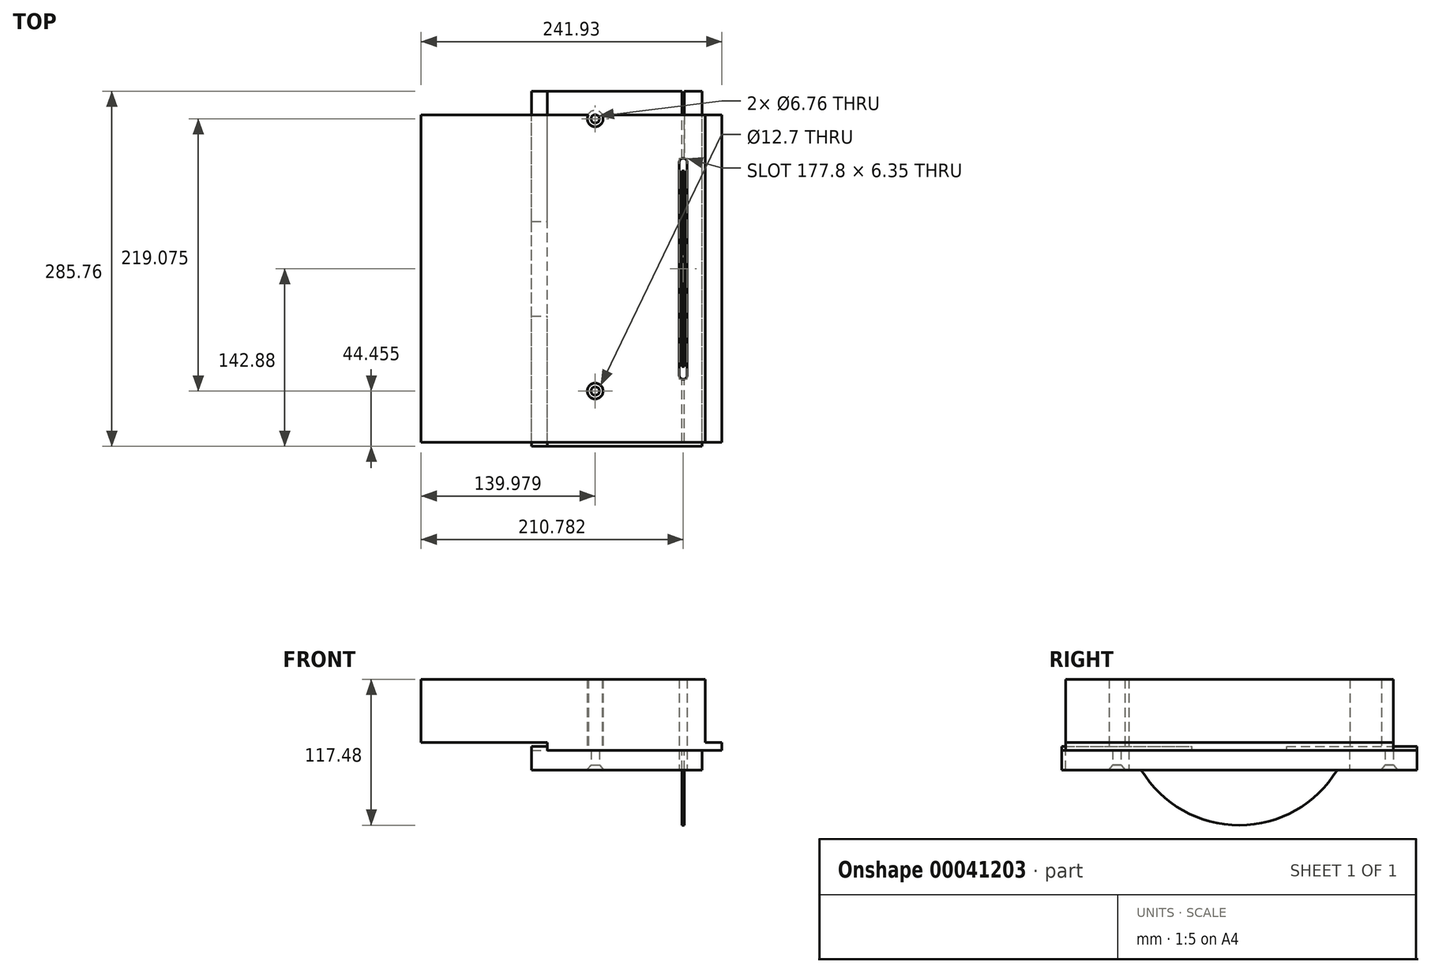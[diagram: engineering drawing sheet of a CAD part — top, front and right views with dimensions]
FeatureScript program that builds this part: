
annotation { "Feature Type Name" : "Feature", "Feature Type Description" : "" }
export const myFeature = defineFeature(function(context is Context, id is Id, definition is map)
    precondition{}
    {
        {
            var Q0;
            Q0=qCreatedBy(makeId("Front.planeOp"),FACE);
            var sketch = newSketch(context, id + "F0", { "sketchPlane" : qUnion([Q0])});
            skLineSegment(sketch, "E0.bottom", {"start": v(0, 0) * mm, "end": v(140.34, 0) * mm});
            skLineSegment(sketch, "E0.top", {"start": v(0, 6.35) * mm, "end": v(140.34, 6.35) * mm});
            skLineSegment(sketch, "E0.left", {"start": v(0, 0) * mm, "end": v(0, 6.35) * mm});
            skLineSegment(sketch, "E0.right", {"start": v(140.34, 0) * mm, "end": v(140.34, 6.35) * mm});
            skLineSegment(sketch, "E1.bottom", {"start": v(127, 6.35) * mm, "end": v(-101.6, 6.35) * mm});
            skLineSegment(sketch, "E1.top", {"start": v(127, 57.15) * mm, "end": v(-101.6, 57.15) * mm});
            skLineSegment(sketch, "E1.left", {"start": v(127, 6.35) * mm, "end": v(127, 57.15) * mm});
            skLineSegment(sketch, "E1.right", {"start": v(-101.6, 6.35) * mm, "end": v(-101.6, 57.15) * mm});
            skLineSegment(sketch, "E2.bottom", {"start": v(108.23, 0) * mm, "end": v(110.13, 0) * mm});
            skLineSegment(sketch, "E2.top", {"start": v(108.23, -60.96) * mm, "end": v(110.13, -60.96) * mm});
            skLineSegment(sketch, "E2.left", {"start": v(108.23, 0) * mm, "end": v(108.23, -60.96) * mm});
            skLineSegment(sketch, "E2.right", {"start": v(110.13, 0) * mm, "end": v(110.13, -60.96) * mm});
            skSolve(sketch);
        }
        {
            var Q0;
            Q0=qSketchRegion(id+"F0",true);
            extrude(context, id + "F1", {"entities" : qUnion([Q0]), "depth" : 139.7 * mm, "hasSecondDirection" : true, "secondDirectionOppositeDirection" : true, "secondDirectionDepth" : 123.82 * mm});
        }
        {
            var Q0;
            Q0=qCreatedBy(makeId("Front.planeOp"),FACE);
            var sketch = newSketch(context, id + "F2", { "sketchPlane" : qUnion([Q0])});
            skLineSegment(sketch, "E3.bottom", {"start": v(0, 0) * mm, "end": v(124.46, 0) * mm});
            skLineSegment(sketch, "E3.top", {"start": v(0, -15.88) * mm, "end": v(124.46, -15.88) * mm});
            skLineSegment(sketch, "E3.left", {"start": v(0, 0) * mm, "end": v(0, -15.88) * mm});
            skLineSegment(sketch, "E3.right", {"start": v(124.46, 0) * mm, "end": v(124.46, -15.88) * mm});
            skLineSegment(sketch, "E4.bottom", {"start": v(0, -15.88) * mm, "end": v(-12.7, -15.88) * mm});
            skLineSegment(sketch, "E4.top", {"start": v(0, 3.18) * mm, "end": v(-12.7, 3.17) * mm});
            skLineSegment(sketch, "E4.left", {"start": v(0, -15.88) * mm, "end": v(0, 3.18) * mm});
            skLineSegment(sketch, "E4.right", {"start": v(-12.7, -15.88) * mm, "end": v(-12.7, 3.17) * mm});
            skSolve(sketch);
        }
        {
            var Q0;
            Q0=makeQuery(id+"F2.imprint","IMPRINT",FACE,{"disambiguationData":[TD([[makeQuery(id+"F2.imprint","IMPRINT",EDGE,{"derivedFrom":sQuery(id+"F2.wireOp",EDGE,"E3.bottom")}),-1.0]])]});
            var Q1;
            {var subQ3=sQuery(id+"F2.wireOp",EDGE,"E4.bottom");Q1=makeQuery(id+"F2.imprint","IMPRINT",FACE,{"disambiguationData":[TD([[makeQuery(id+"F2.imprint","IMPRINT",EDGE,{"derivedFrom":subQ3}),-1.0]])]});}
            var Q2;
            Q2=makeQuery(id+"F1.opExtrude","CAP_FACE",FACE,{"disambiguationData":[OSD([sQuery(id+"F0.wireOp",EDGE,"E0.bottom"),sQuery(id+"F0.wireOp",EDGE,"E0.top"),sQuery(id+"F0.wireOp",EDGE,"E0.left"),sQuery(id+"F0.wireOp",EDGE,"E0.right"),sQuery(id+"F0.wireOp",EDGE,"E1.bottom"),sQuery(id+"F0.wireOp",EDGE,"E1.top"),sQuery(id+"F0.wireOp",EDGE,"E1.left"),sQuery(id+"F0.wireOp",EDGE,"E1.right"),sQuery(id+"F0.wireOp",EDGE,"E2.top"),sQuery(id+"F0.wireOp",EDGE,"E2.left"),sQuery(id+"F0.wireOp",EDGE,"E2.right")])],"isStart":true});
            extrude(context, id + "F3", {"entities" : qUnion([Q0, Q1]), "depth" : 142.88 * mm, "hasSecondDirection" : true, "secondDirectionOppositeDirection" : true, "secondDirectionBoundEntityFace" : qUnion([Q2]), "secondDirectionDepth" : 142.88 * mm});
        }
        {
            var Q0;
            Q0=makeQuery(id+"F3.opExtrude","SWEPT_FACE",FACE,{"disambiguationData":[OSD([sQuery(id+"F2.wireOp",EDGE,"E3.top")])]});
            var sketch = newSketch(context, id + "F4", { "sketchPlane" : qUnion([Q0])});
            skLineSegment(sketch, "E5.bottom", {"start": v(109.18, -88.9) * mm, "end": v(109.18, -88.9) * mm});
            skLineSegment(sketch, "E5.top", {"start": v(109.18, 88.9) * mm, "end": v(109.18, 88.9) * mm});
            skLineSegment(sketch, "E5.left", {"start": v(112.36, 85.73) * mm, "end": v(112.36, -85.73) * mm});
            skLineSegment(sketch, "E5.right", {"start": v(106, 85.73) * mm, "end": v(106, -85.73) * mm});
            skArc(sketch, "E6.filletArc", {"start": v(109.18, 88.9) * mm, "mid": v(106.94, 87.97) * mm, "end": v(106, 85.73) * mm});
            skArc(sketch, "E7.filletArc", {"start": v(112.36, 85.73) * mm, "mid": v(111.43, 87.97) * mm, "end": v(109.18, 88.9) * mm});
            skArc(sketch, "E8.filletArc", {"start": v(109.18, -88.9) * mm, "mid": v(111.43, -87.97) * mm, "end": v(112.36, -85.73) * mm});
            skArc(sketch, "E9.filletArc", {"start": v(106, -85.73) * mm, "mid": v(106.94, -87.97) * mm, "end": v(109.18, -88.9) * mm});
            skSolve(sketch);
        }
        {
            var Q0;
            Q0=makeQuery(id+"F1.opExtrude","SWEPT_FACE",FACE,{"disambiguationData":[OSD([sQuery(id+"F0.wireOp",EDGE,"E2.right")])]});
            var sketch = newSketch(context, id + "F5", { "sketchPlane" : qUnion([Q0])});
            skLineSegment(sketch, "E10.0", {"start": v(-139.7, 0) * mm, "end": v(-139.7, -60.96) * mm});
            skLineSegment(sketch, "E11.0", {"start": v(123.83, 0) * mm, "end": v(123.83, -60.96) * mm});
            skLineSegment(sketch, "E12", {"start": v(0, 0) * mm, "end": v(0, 82.53) * mm, "construction": true});
            skLineSegment(sketch, "E13", {"start": v(-86.43, 0) * mm, "end": v(-139.7, 0) * mm});
            skLineSegment(sketch, "E14", {"start": v(-139.7, 0) * mm, "end": v(-139.7, -88.9) * mm});
            skLineSegment(sketch, "E15", {"start": v(-139.7, -88.9) * mm, "end": v(152.4, -88.9) * mm});
            skLineSegment(sketch, "E16", {"start": v(152.4, -88.9) * mm, "end": v(152.4, 0) * mm});
            skLineSegment(sketch, "E17", {"start": v(152.4, 0) * mm, "end": v(86.43, 0) * mm});
            skArc(sketch, "E18.converted", {"start": v(-86.43, 0) * mm, "mid": v(0, -60.33) * mm, "end": v(86.43, 0) * mm});
            skSolve(sketch);
        }
        {
            var Q0;
            Q0=qSketchRegion(id+"F5",true);
            var Q1;
            Q1=makeQuery(id+"F1.opExtrude","SWEPT_FACE",FACE,{"disambiguationData":[OSD([sQuery(id+"F0.wireOp",EDGE,"E2.left")])]});
            extrude(context, id + "F6", {"entities" : qUnion([Q0]), "operationType" : NewBodyOperationType.REMOVE, "endBound" : BoundingType.UP_TO_SURFACE, "oppositeDirection" : true, "endBoundEntityFace" : qUnion([Q1]), "depth" : 5.08 * mm});
        }
        {
            var Q0;
            {var subQ0=sQuery(id+"F0.wireOp",EDGE,"E0.bottom");Q0=makeQuery(id+"F6.boolean.opBoolean","MERGE",FACE,{"derivedFrom":[makeQuery(id+"F1.opExtrude","SWEPT_FACE",FACE,{"disambiguationData":[OSD([subQ0]),TDD([makeQuery(id+"F0.imprint","IMPRINT",EDGE,{"disambiguationData":[TD([[makeQuery(id+"F0.imprint","INTERSECT",VERTEX,{"derivedFrom":[subQ0,sQuery(id+"F0.wireOp",EDGE,"E0.left")]}),-1.0]])],"derivedFrom":subQ0})])]}),makeQuery(id+"F1.opExtrude","SWEPT_FACE",FACE,{"disambiguationData":[OSD([subQ0]),TDD([makeQuery(id+"F0.imprint","IMPRINT",EDGE,{"disambiguationData":[TD([[makeQuery(id+"F0.imprint","INTERSECT",VERTEX,{"derivedFrom":[subQ0,sQuery(id+"F0.wireOp",EDGE,"E0.right")]}),1.0]])],"derivedFrom":subQ0})])]}),makeQuery(id+"F6.opExtrude","SWEPT_FACE",FACE,{"disambiguationData":[OSD([sQuery(id+"F5.wireOp",EDGE,"E13")])]}),makeQuery(id+"F6.opExtrude","SWEPT_FACE",FACE,{"disambiguationData":[OSD([sQuery(id+"F5.wireOp",EDGE,"E17")])]})]});}
            var sketch = newSketch(context, id + "F7", { "sketchPlane" : qUnion([Q0])});
            skCircle(sketch, "E19", {"center": v(38.38, -120.65) * mm, "radius": 6.35 * mm});
            skCircle(sketch, "E20", {"center": v(38.38, 98.43) * mm, "radius": 6.35 * mm});
            skSolve(sketch);
        }
        {
            var Q0;
            Q0=qSketchRegion(id+"F7",true);
            var Q1;
            Q1=makeQuery(id+"F1.opExtrude","SWEPT_FACE",FACE,{"disambiguationData":[OSD([sQuery(id+"F0.wireOp",EDGE,"E1.top")])]});
            extrude(context, id + "F8", {"entities" : qUnion([Q0]), "operationType" : NewBodyOperationType.REMOVE, "endBound" : BoundingType.UP_TO_SURFACE, "oppositeDirection" : true, "endBoundEntityFace" : qUnion([Q1]), "depth" : 25.4 * mm});
        }
        {
            var Q0;
            Q0=makeQuery(id+"F7.imprint","IMPRINT",FACE,{"disambiguationData":[TD([[makeQuery(id+"F7.imprint","IMPRINT",EDGE,{"derivedFrom":sQuery(id+"F7.wireOp",EDGE,"E19")}),-1.0]])]});
            var sketch = newSketch(context, id + "F9", { "sketchPlane" : qUnion([Q0])});
            skPoint(sketch, "E21.0", {"position": v(38.38, 98.43) * mm});
            skPoint(sketch, "E22.0", {"position": v(38.38, -120.65) * mm});
            skSolve(sketch);
        }
        {
            var Q0;
            Q0=makeQuery(id+"F3.opExtrude","SWEPT_FACE",FACE,{"disambiguationData":[OSD([sQuery(id+"F2.wireOp",EDGE,"E3.top"),sQuery(id+"F2.wireOp",EDGE,"E4.bottom")])]});
            var sketch = newSketch(context, id + "F10", { "sketchPlane" : qUnion([Q0])});
            skPoint(sketch, "E23.0", {"position": v(38.38, -120.65) * mm});
            skPoint(sketch, "E24.0", {"position": v(38.38, 98.43) * mm});
            skSolve(sketch);
        }
        {
            var Q0;
            Q0=sQuery(id+"F10.wireOp",VERTEX,"E23.0");
            var Q1;
            Q1=sQuery(id+"F10.wireOp",VERTEX,"E24.0");
            var Q2;
            Q2=makeQuery(id+"F3.opExtrude","SWEPT_BODY",BODY,{"disambiguationData":[OSD([sQuery(id+"F2.wireOp",EDGE,"E3.bottom"),sQuery(id+"F2.wireOp",EDGE,"E3.top"),sQuery(id+"F2.wireOp",EDGE,"E3.right"),sQuery(id+"F2.wireOp",EDGE,"E4.bottom"),sQuery(id+"F2.wireOp",EDGE,"E4.top"),sQuery(id+"F2.wireOp",EDGE,"E4.left"),sQuery(id+"F2.wireOp",EDGE,"E4.right")])]});
            hole(context, id + "F11", {"style" : HoleStyle.C_SINK, "endStyle" : HoleEndStyle.THROUGH, "standardTappedOrClearance" : lookupTablePath({ "standard" : "ANSI", "fit" : "Normal (ASME)", "size" : "1/4", "type" : "Clearance" }), "standardBlindInLast" : lookupTablePath({ "fit" : "Free", "standard" : "ANSI", "size" : "1/4", "type" : "Clearance" }), "holeDiameter" : 6.76 * mm, "cSinkDiameter" : 13.5 * mm, "cSinkAngle" : 82 * degree, "locations" : qUnion([Q0, Q1]), "scope" : qUnion([Q2]), "isTappedThrough" : true});
        }
        {
            var Q0;
            Q0=qSketchRegion(id+"F4",true);
            var Q1;
            Q1=makeQuery(id+"F1.opExtrude","SWEPT_BODY",BODY,{"disambiguationData":[OSD([sQuery(id+"F0.wireOp",EDGE,"E0.bottom"),sQuery(id+"F0.wireOp",EDGE,"E0.top"),sQuery(id+"F0.wireOp",EDGE,"E0.left"),sQuery(id+"F0.wireOp",EDGE,"E0.right"),sQuery(id+"F0.wireOp",EDGE,"E1.bottom"),sQuery(id+"F0.wireOp",EDGE,"E1.top"),sQuery(id+"F0.wireOp",EDGE,"E1.left"),sQuery(id+"F0.wireOp",EDGE,"E1.right"),sQuery(id+"F0.wireOp",EDGE,"E2.top"),sQuery(id+"F0.wireOp",EDGE,"E2.left"),sQuery(id+"F0.wireOp",EDGE,"E2.right")])]});
            extrude(context, id + "F12", {"entities" : qUnion([Q0]), "operationType" : NewBodyOperationType.REMOVE, "endBound" : BoundingType.UP_TO_BODY, "oppositeDirection" : true, "endBoundEntityBody" : qUnion([Q1]), "depth" : 25.4 * mm});
        }
        {
            var Q0;
            Q0=makeQuery(id+"F3.opExtrude","SWEPT_FACE",FACE,{"disambiguationData":[OSD([sQuery(id+"F2.wireOp",EDGE,"E4.left")])]});
            var sketch = newSketch(context, id + "F13", { "sketchPlane" : qUnion([Q0])});
            skLineSegment(sketch, "E25.bottom", {"start": v(0, 0) * mm, "end": v(38.1, 0) * mm});
            skLineSegment(sketch, "E25.top", {"start": v(0, 3.18) * mm, "end": v(38.1, 3.18) * mm});
            skLineSegment(sketch, "E25.right", {"start": v(38.1, 0) * mm, "end": v(38.1, 3.18) * mm});
            skLineSegment(sketch, "E26.MirrorCS", {"start": v(-38.1, 0) * mm, "end": v(-38.1, 3.18) * mm});
            skLineSegment(sketch, "E27.MirrorCS", {"start": v(0, 0) * mm, "end": v(-38.1, 0) * mm});
            skLineSegment(sketch, "E28.MirrorCS", {"start": v(0, 3.18) * mm, "end": v(-38.1, 3.18) * mm});
            skSolve(sketch);
        }
        {
            var Q0;
            Q0=makeQuery(id+"F13.imprint","IMPRINT",FACE,{"disambiguationData":[TD([[makeQuery(id+"F13.imprint","IMPRINT",EDGE,{"derivedFrom":sQuery(id+"F13.wireOp",EDGE,"E25.bottom")}),1.0]])]});
            var Q1;
            Q1=makeQuery(id+"F3.opExtrude","SWEPT_FACE",FACE,{"disambiguationData":[OSD([sQuery(id+"F2.wireOp",EDGE,"E4.right")])]});
            extrude(context, id + "F14", {"entities" : qUnion([Q0]), "operationType" : NewBodyOperationType.REMOVE, "endBound" : BoundingType.UP_TO_SURFACE, "oppositeDirection" : true, "endBoundEntityFace" : qUnion([Q1]), "depth" : 25.4 * mm});
        }
    });
